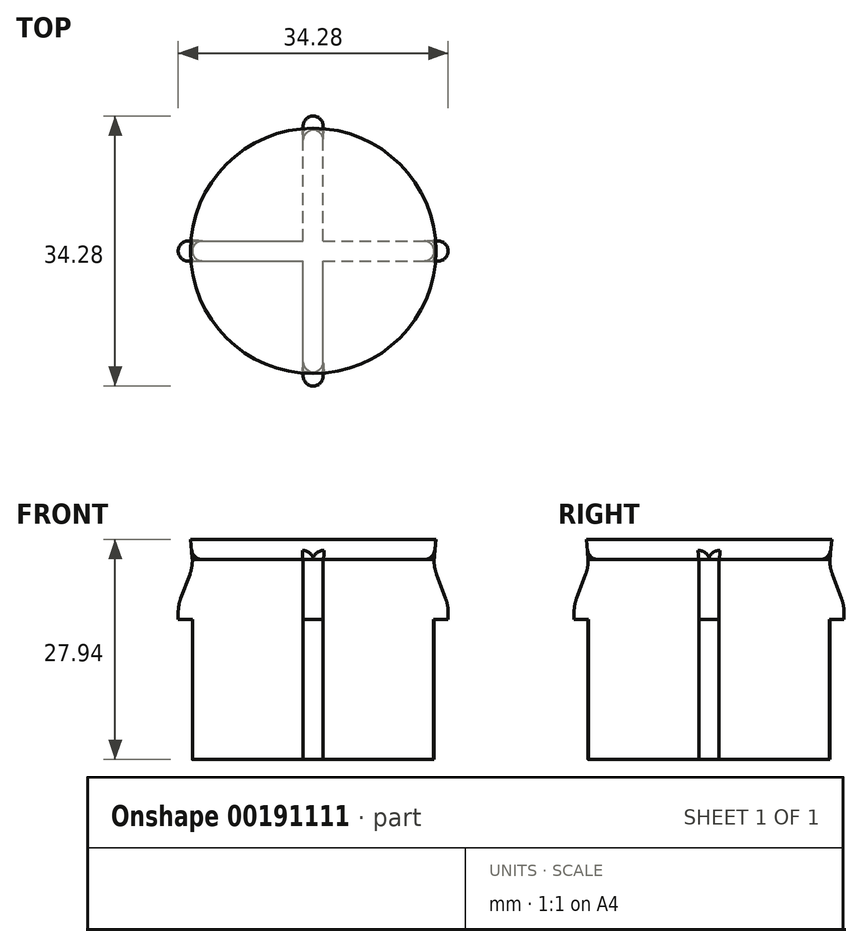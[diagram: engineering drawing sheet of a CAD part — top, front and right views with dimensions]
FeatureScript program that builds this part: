
annotation { "Feature Type Name" : "Feature", "Feature Type Description" : "" }
export const myFeature = defineFeature(function(context is Context, id is Id, definition is map)
    precondition{}
    {
        {
            var Q0;
            Q0=qCreatedBy(makeId("Top.planeOp"),FACE);
            var sketch = newSketch(context, id + "F0", { "sketchPlane" : qUnion([Q0])});
            skCircle(sketch, "E0", {"center": v(0, 0) * mm, "radius": 15.37 * mm});
            skSolve(sketch);
        }
        {
            var Q0;
            Q0 = qSketchRegion(id + "F0", true);
            extrude(context, id + "F1", {"entities" : qUnion([Q0]), "depth" : 2.54 * mm, "hasDraft" : true, "draftAngle" : 5 * degree});
        }
        {
            var Q0;
            Q0=makeQuery(id+"F1.opExtrude","CAP_FACE",FACE,{"disambiguationData":[OSD([sQuery(id+"F0.wireOp",EDGE,"E0")])],"isStart":true});
            var sketch = newSketch(context, id + "F2", { "sketchPlane" : qUnion([Q0])});
            skLineSegment(sketch, "E1.left", {"start": v(-1.27, 15.3) * mm, "end": v(-1.27, 1.27) * mm});
            skLineSegment(sketch, "E1.right", {"start": v(1.27, 15.3) * mm, "end": v(1.27, 1.27) * mm});
            skLineSegment(sketch, "E2.bottom", {"start": v(-15.3, 1.27) * mm, "end": v(-1.27, 1.27) * mm});
            skLineSegment(sketch, "E2.top", {"start": v(-15.3, -1.27) * mm, "end": v(-1.27, -1.27) * mm});
            skLineSegment(sketch, "E3.trimOffspring", {"start": v(1.27, 1.27) * mm, "end": v(15.3, 1.27) * mm});
            skLineSegment(sketch, "E4.trimOffspring", {"start": v(1.27, -1.27) * mm, "end": v(1.27, -15.3) * mm});
            skLineSegment(sketch, "E5.trimOffspring", {"start": v(1.27, -1.27) * mm, "end": v(15.3, -1.27) * mm});
            skLineSegment(sketch, "E6.trimOffspring", {"start": v(-1.27, -1.27) * mm, "end": v(-1.27, -15.3) * mm});
            skArc(sketch, "E7", {"start": v(1.27, 15.3) * mm, "mid": v(0, 15.35) * mm, "end": v(-1.27, 15.3) * mm});
            skArc(sketch, "E8.trimOffspring", {"start": v(15.3, -1.27) * mm, "mid": v(15.35, 0) * mm, "end": v(15.3, 1.27) * mm});
            skArc(sketch, "E9.trimOffspring", {"start": v(-1.27, -15.3) * mm, "mid": v(0, -15.35) * mm, "end": v(1.27, -15.3) * mm});
            skArc(sketch, "E10.trimOffspring", {"start": v(-15.3, 1.27) * mm, "mid": v(-15.35, 0) * mm, "end": v(-15.3, -1.27) * mm});
            skSolve(sketch);
        }
        {
            var Q0;
            Q0 = qSketchRegion(id + "F2", true);
            extrude(context, id + "F3", {"entities" : qUnion([Q0]), "operationType" : NewBodyOperationType.ADD, "depth" : 25.4 * mm});
        }
        {
            var Q0;
            Q0 = qSketchRegion(id + "F2", true);
            extrude(context, id + "F4", {"entities" : qUnion([Q0]), "operationType" : NewBodyOperationType.ADD, "depth" : 25.4 * mm});
        }
        {
            var Q0;
            Q0=qCreatedBy(makeId("Top.planeOp"),FACE);
            cPlane(context, id + "F5", {"entities" : qUnion([Q0]), "cplaneType" : CPlaneType.OFFSET, "offset" : 7.62 * mm, "oppositeDirection" : true, "width" : 152.4 * mm, "height" : 152.4 * mm});
        }
        {
            var Q0;
            Q0=qCreatedBy(id+"F5.planeOp",FACE);
            var sketch = newSketch(context, id + "F6", { "sketchPlane" : qUnion([Q0])});
            skArc(sketch, "E11", {"start": v(-1.27, -17.1) * mm, "mid": v(0, -17.15) * mm, "end": v(1.27, -17.1) * mm});
            skLineSegment(sketch, "E12.left", {"start": v(-1.27, -17.1) * mm, "end": v(-1.27, 17.1) * mm});
            skLineSegment(sketch, "E12.right", {"start": v(1.27, -17.1) * mm, "end": v(1.27, 17.1) * mm});
            skLineSegment(sketch, "E13.bottom", {"start": v(-17.1, -1.27) * mm, "end": v(17.1, -1.27) * mm});
            skLineSegment(sketch, "E13.top", {"start": v(-17.1, 1.27) * mm, "end": v(17.1, 1.27) * mm});
            skArc(sketch, "E14.trimOffspring", {"start": v(17.1, -1.27) * mm, "mid": v(17.15, 0) * mm, "end": v(17.1, 1.27) * mm});
            skArc(sketch, "E15.trimOffspring", {"start": v(1.27, 17.1) * mm, "mid": v(0, 17.15) * mm, "end": v(-1.27, 17.1) * mm});
            skArc(sketch, "E16.trimOffspring", {"start": v(-17.1, 1.27) * mm, "mid": v(-17.15, 0) * mm, "end": v(-17.1, -1.27) * mm});
            skSolve(sketch);
        }
        {
            var Q0;
            Q0 = qSketchRegion(id + "F6", true);
            extrude(context, id + "F7", {"entities" : qUnion([Q0]), "operationType" : NewBodyOperationType.ADD, "depth" : 1.52 * mm});
        }
        {
            var Q0;
            Q0=makeQuery(id+"F7.boolean.opBoolean","INTERSECT",EDGE,{"derivedFrom":[makeQuery(id+"F3.opExtrude","SWEPT_FACE",FACE,{"disambiguationData":[OSD([sQuery(id+"F2.wireOp",EDGE,"E7")])]}),makeQuery(id+"F7.opExtrude","CAP_FACE",FACE,{"disambiguationData":[OSD([sQuery(id+"F6.wireOp",EDGE,"E11"),sQuery(id+"F6.wireOp",EDGE,"E12.left"),sQuery(id+"F6.wireOp",EDGE,"E12.right"),sQuery(id+"F6.wireOp",EDGE,"E13.bottom"),sQuery(id+"F6.wireOp",EDGE,"E13.top"),sQuery(id+"F6.wireOp",EDGE,"E14.trimOffspring"),sQuery(id+"F6.wireOp",EDGE,"E15.trimOffspring"),sQuery(id+"F6.wireOp",EDGE,"E16.trimOffspring")])],"isStart":false})]});
            chamfer(context, id + "F8", {"entities" : qUnion([Q0]), "chamferType" : ChamferType.TWO_OFFSETS, "width1" : 5.08 * mm, "oppositeDirection" : false, "width2" : 1.9 * mm, "tangentPropagation" : true});
        }
        {
            var Q0;
            Q0=makeQuery(id+"F7.boolean.opBoolean","INTERSECT",EDGE,{"derivedFrom":[makeQuery(id+"F3.opExtrude","SWEPT_FACE",FACE,{"disambiguationData":[OSD([sQuery(id+"F2.wireOp",EDGE,"E8.trimOffspring")])]}),makeQuery(id+"F7.opExtrude","CAP_FACE",FACE,{"disambiguationData":[OSD([sQuery(id+"F6.wireOp",EDGE,"E11"),sQuery(id+"F6.wireOp",EDGE,"E12.left"),sQuery(id+"F6.wireOp",EDGE,"E12.right"),sQuery(id+"F6.wireOp",EDGE,"E13.bottom"),sQuery(id+"F6.wireOp",EDGE,"E13.top"),sQuery(id+"F6.wireOp",EDGE,"E14.trimOffspring"),sQuery(id+"F6.wireOp",EDGE,"E15.trimOffspring"),sQuery(id+"F6.wireOp",EDGE,"E16.trimOffspring")])],"isStart":false})]});
            chamfer(context, id + "F9", {"entities" : qUnion([Q0]), "chamferType" : ChamferType.TWO_OFFSETS, "width1" : 5.08 * mm, "oppositeDirection" : false, "width2" : 1.9 * mm, "tangentPropagation" : true});
        }
        {
            var Q0;
            Q0=makeQuery(id+"F7.boolean.opBoolean","INTERSECT",EDGE,{"derivedFrom":[makeQuery(id+"F3.opExtrude","SWEPT_FACE",FACE,{"disambiguationData":[OSD([sQuery(id+"F2.wireOp",EDGE,"E9.trimOffspring")])]}),makeQuery(id+"F7.opExtrude","CAP_FACE",FACE,{"disambiguationData":[OSD([sQuery(id+"F6.wireOp",EDGE,"E11"),sQuery(id+"F6.wireOp",EDGE,"E12.left"),sQuery(id+"F6.wireOp",EDGE,"E12.right"),sQuery(id+"F6.wireOp",EDGE,"E13.bottom"),sQuery(id+"F6.wireOp",EDGE,"E13.top"),sQuery(id+"F6.wireOp",EDGE,"E14.trimOffspring"),sQuery(id+"F6.wireOp",EDGE,"E15.trimOffspring"),sQuery(id+"F6.wireOp",EDGE,"E16.trimOffspring")])],"isStart":false})]});
            chamfer(context, id + "F10", {"entities" : qUnion([Q0]), "chamferType" : ChamferType.TWO_OFFSETS, "width1" : 5.08 * mm, "oppositeDirection" : false, "width2" : 1.9 * mm, "tangentPropagation" : true});
        }
        {
            var Q0;
            Q0=makeQuery(id+"F7.boolean.opBoolean","INTERSECT",EDGE,{"derivedFrom":[makeQuery(id+"F3.opExtrude","SWEPT_FACE",FACE,{"disambiguationData":[OSD([sQuery(id+"F2.wireOp",EDGE,"E10.trimOffspring")])]}),makeQuery(id+"F7.opExtrude","CAP_FACE",FACE,{"disambiguationData":[OSD([sQuery(id+"F6.wireOp",EDGE,"E11"),sQuery(id+"F6.wireOp",EDGE,"E12.left"),sQuery(id+"F6.wireOp",EDGE,"E12.right"),sQuery(id+"F6.wireOp",EDGE,"E13.bottom"),sQuery(id+"F6.wireOp",EDGE,"E13.top"),sQuery(id+"F6.wireOp",EDGE,"E14.trimOffspring"),sQuery(id+"F6.wireOp",EDGE,"E15.trimOffspring"),sQuery(id+"F6.wireOp",EDGE,"E16.trimOffspring")])],"isStart":false})]});
            chamfer(context, id + "F11", {"entities" : qUnion([Q0]), "chamferType" : ChamferType.TWO_OFFSETS, "width1" : 5.08 * mm, "oppositeDirection" : false, "width2" : 1.9 * mm, "tangentPropagation" : true});
        }
        {
            var Q0;
            {var subQ0=sQuery(id+"F6.wireOp",EDGE,"E13.bottom");var subQ1=sQuery(id+"F6.wireOp",EDGE,"E12.right");var subQ2=sQuery(id+"F6.wireOp",EDGE,"E12.left");var subQ3=sQuery(id+"F6.wireOp",EDGE,"E11");var subQ4=makeQuery(id+"F7.opExtrude","CAP_FACE",FACE,{"disambiguationData":[OSD([subQ3,subQ2,subQ1,subQ0,sQuery(id+"F6.wireOp",EDGE,"E13.top"),sQuery(id+"F6.wireOp",EDGE,"E14.trimOffspring"),sQuery(id+"F6.wireOp",EDGE,"E15.trimOffspring"),sQuery(id+"F6.wireOp",EDGE,"E16.trimOffspring")])],"isStart":false});var subQ5=makeQuery(id+"F3.opExtrude","SWEPT_FACE",FACE,{"disambiguationData":[OSD([sQuery(id+"F2.wireOp",EDGE,"E7")])]});Q0=makeQuery(id+"F8.opChamfer","BLEND_EDGE",EDGE,{"blendedFrom":[makeQuery(id+"F7.boolean.opBoolean","INTERSECT",EDGE,{"derivedFrom":[subQ5,subQ4]}),makeQuery(id+"F7.boolean.opBoolean","SPLIT",FACE,{"disambiguationData":[TD([makeQuery(id+"F1.opExtrude","CAP_FACE",FACE,{"disambiguationData":[OSD([sQuery(id+"F0.wireOp",EDGE,"E0")])],"isStart":true})])],"derivedFrom":subQ5})],"blendedInto":[makeQuery(id+"F7.boolean.opBoolean","SPLIT",FACE,{"disambiguationData":[TD([makeQuery(id+"F1.opExtrude","CAP_FACE",FACE,{"disambiguationData":[OSD([sQuery(id+"F0.wireOp",EDGE,"E0")])],"isStart":true})])],"derivedFrom":subQ5})]});}
            var Q1;
            {var subQ0=sQuery(id+"F6.wireOp",EDGE,"E14.trimOffspring");var subQ1=sQuery(id+"F6.wireOp",EDGE,"E13.top");var subQ2=sQuery(id+"F6.wireOp",EDGE,"E13.bottom");var subQ3=sQuery(id+"F6.wireOp",EDGE,"E12.right");var subQ4=makeQuery(id+"F7.opExtrude","CAP_FACE",FACE,{"disambiguationData":[OSD([sQuery(id+"F6.wireOp",EDGE,"E11"),sQuery(id+"F6.wireOp",EDGE,"E12.left"),subQ3,subQ2,subQ1,subQ0,sQuery(id+"F6.wireOp",EDGE,"E15.trimOffspring"),sQuery(id+"F6.wireOp",EDGE,"E16.trimOffspring")])],"isStart":false});var subQ5=makeQuery(id+"F3.opExtrude","SWEPT_FACE",FACE,{"disambiguationData":[OSD([sQuery(id+"F2.wireOp",EDGE,"E8.trimOffspring")])]});Q1=makeQuery(id+"F9.opChamfer","BLEND_EDGE",EDGE,{"blendedFrom":[makeQuery(id+"F7.boolean.opBoolean","INTERSECT",EDGE,{"derivedFrom":[subQ5,subQ4]}),makeQuery(id+"F7.boolean.opBoolean","SPLIT",FACE,{"disambiguationData":[TD([makeQuery(id+"F1.opExtrude","CAP_FACE",FACE,{"disambiguationData":[OSD([sQuery(id+"F0.wireOp",EDGE,"E0")])],"isStart":true})])],"derivedFrom":subQ5})],"blendedInto":[makeQuery(id+"F7.boolean.opBoolean","SPLIT",FACE,{"disambiguationData":[TD([makeQuery(id+"F1.opExtrude","CAP_FACE",FACE,{"disambiguationData":[OSD([sQuery(id+"F0.wireOp",EDGE,"E0")])],"isStart":true})])],"derivedFrom":subQ5})]});}
            var Q2;
            {var subQ0=sQuery(id+"F6.wireOp",EDGE,"E15.trimOffspring");var subQ1=sQuery(id+"F6.wireOp",EDGE,"E13.top");var subQ2=sQuery(id+"F6.wireOp",EDGE,"E12.right");var subQ3=sQuery(id+"F6.wireOp",EDGE,"E12.left");var subQ4=makeQuery(id+"F7.opExtrude","CAP_FACE",FACE,{"disambiguationData":[OSD([sQuery(id+"F6.wireOp",EDGE,"E11"),subQ3,subQ2,sQuery(id+"F6.wireOp",EDGE,"E13.bottom"),subQ1,sQuery(id+"F6.wireOp",EDGE,"E14.trimOffspring"),subQ0,sQuery(id+"F6.wireOp",EDGE,"E16.trimOffspring")])],"isStart":false});var subQ5=makeQuery(id+"F3.opExtrude","SWEPT_FACE",FACE,{"disambiguationData":[OSD([sQuery(id+"F2.wireOp",EDGE,"E9.trimOffspring")])]});Q2=makeQuery(id+"F10.opChamfer","BLEND_EDGE",EDGE,{"blendedFrom":[makeQuery(id+"F7.boolean.opBoolean","INTERSECT",EDGE,{"derivedFrom":[subQ5,subQ4]}),makeQuery(id+"F7.boolean.opBoolean","SPLIT",FACE,{"disambiguationData":[TD([makeQuery(id+"F1.opExtrude","CAP_FACE",FACE,{"disambiguationData":[OSD([sQuery(id+"F0.wireOp",EDGE,"E0")])],"isStart":true})])],"derivedFrom":subQ5})],"blendedInto":[makeQuery(id+"F7.boolean.opBoolean","SPLIT",FACE,{"disambiguationData":[TD([makeQuery(id+"F1.opExtrude","CAP_FACE",FACE,{"disambiguationData":[OSD([sQuery(id+"F0.wireOp",EDGE,"E0")])],"isStart":true})])],"derivedFrom":subQ5})]});}
            var Q3;
            {var subQ0=sQuery(id+"F6.wireOp",EDGE,"E16.trimOffspring");var subQ1=sQuery(id+"F6.wireOp",EDGE,"E13.top");var subQ2=sQuery(id+"F6.wireOp",EDGE,"E13.bottom");var subQ3=sQuery(id+"F6.wireOp",EDGE,"E12.left");var subQ4=makeQuery(id+"F7.opExtrude","CAP_FACE",FACE,{"disambiguationData":[OSD([sQuery(id+"F6.wireOp",EDGE,"E11"),subQ3,sQuery(id+"F6.wireOp",EDGE,"E12.right"),subQ2,subQ1,sQuery(id+"F6.wireOp",EDGE,"E14.trimOffspring"),sQuery(id+"F6.wireOp",EDGE,"E15.trimOffspring"),subQ0])],"isStart":false});var subQ5=makeQuery(id+"F3.opExtrude","SWEPT_FACE",FACE,{"disambiguationData":[OSD([sQuery(id+"F2.wireOp",EDGE,"E10.trimOffspring")])]});Q3=makeQuery(id+"F11.opChamfer","BLEND_EDGE",EDGE,{"blendedFrom":[makeQuery(id+"F7.boolean.opBoolean","INTERSECT",EDGE,{"derivedFrom":[subQ5,subQ4]}),makeQuery(id+"F7.boolean.opBoolean","SPLIT",FACE,{"disambiguationData":[TD([makeQuery(id+"F1.opExtrude","CAP_FACE",FACE,{"disambiguationData":[OSD([sQuery(id+"F0.wireOp",EDGE,"E0")])],"isStart":true})])],"derivedFrom":subQ5})],"blendedInto":[makeQuery(id+"F7.boolean.opBoolean","SPLIT",FACE,{"disambiguationData":[TD([makeQuery(id+"F1.opExtrude","CAP_FACE",FACE,{"disambiguationData":[OSD([sQuery(id+"F0.wireOp",EDGE,"E0")])],"isStart":true})])],"derivedFrom":subQ5})]});}
            fillet(context, id + "F12", {"entities" : qUnion([Q0, Q1, Q2, Q3]), "radius" : 5.08 * mm, "tangentPropagation" : true, "allowEdgeOverflow" : false});
        }
        {
            var Q0;
            {var subQ0=sQuery(id+"F6.wireOp",EDGE,"E11");Q0=makeQuery(id+"F8.opChamfer","BLEND_EDGE",EDGE,{"blendedFrom":[makeQuery(id+"F7.boolean.opBoolean","INTERSECT",EDGE,{"derivedFrom":[makeQuery(id+"F3.opExtrude","SWEPT_FACE",FACE,{"disambiguationData":[OSD([sQuery(id+"F2.wireOp",EDGE,"E7")])]}),makeQuery(id+"F7.opExtrude","CAP_FACE",FACE,{"disambiguationData":[OSD([subQ0,sQuery(id+"F6.wireOp",EDGE,"E12.left"),sQuery(id+"F6.wireOp",EDGE,"E12.right"),sQuery(id+"F6.wireOp",EDGE,"E13.bottom"),sQuery(id+"F6.wireOp",EDGE,"E13.top"),sQuery(id+"F6.wireOp",EDGE,"E14.trimOffspring"),sQuery(id+"F6.wireOp",EDGE,"E15.trimOffspring"),sQuery(id+"F6.wireOp",EDGE,"E16.trimOffspring")])],"isStart":false})]}),makeQuery(id+"F7.opExtrude","SWEPT_FACE",FACE,{"disambiguationData":[OSD([subQ0])]})],"blendedInto":[makeQuery(id+"F7.opExtrude","SWEPT_FACE",FACE,{"disambiguationData":[OSD([subQ0])]})]});}
            var Q1;
            {var subQ0=sQuery(id+"F6.wireOp",EDGE,"E16.trimOffspring");Q1=makeQuery(id+"F11.opChamfer","BLEND_EDGE",EDGE,{"blendedFrom":[makeQuery(id+"F7.boolean.opBoolean","INTERSECT",EDGE,{"derivedFrom":[makeQuery(id+"F3.opExtrude","SWEPT_FACE",FACE,{"disambiguationData":[OSD([sQuery(id+"F2.wireOp",EDGE,"E10.trimOffspring")])]}),makeQuery(id+"F7.opExtrude","CAP_FACE",FACE,{"disambiguationData":[OSD([sQuery(id+"F6.wireOp",EDGE,"E11"),sQuery(id+"F6.wireOp",EDGE,"E12.left"),sQuery(id+"F6.wireOp",EDGE,"E12.right"),sQuery(id+"F6.wireOp",EDGE,"E13.bottom"),sQuery(id+"F6.wireOp",EDGE,"E13.top"),sQuery(id+"F6.wireOp",EDGE,"E14.trimOffspring"),sQuery(id+"F6.wireOp",EDGE,"E15.trimOffspring"),subQ0])],"isStart":false})]}),makeQuery(id+"F7.opExtrude","SWEPT_FACE",FACE,{"disambiguationData":[OSD([subQ0])]})],"blendedInto":[makeQuery(id+"F7.opExtrude","SWEPT_FACE",FACE,{"disambiguationData":[OSD([subQ0])]})]});}
            var Q2;
            {var subQ0=sQuery(id+"F6.wireOp",EDGE,"E15.trimOffspring");Q2=makeQuery(id+"F10.opChamfer","BLEND_EDGE",EDGE,{"blendedFrom":[makeQuery(id+"F7.boolean.opBoolean","INTERSECT",EDGE,{"derivedFrom":[makeQuery(id+"F3.opExtrude","SWEPT_FACE",FACE,{"disambiguationData":[OSD([sQuery(id+"F2.wireOp",EDGE,"E9.trimOffspring")])]}),makeQuery(id+"F7.opExtrude","CAP_FACE",FACE,{"disambiguationData":[OSD([sQuery(id+"F6.wireOp",EDGE,"E11"),sQuery(id+"F6.wireOp",EDGE,"E12.left"),sQuery(id+"F6.wireOp",EDGE,"E12.right"),sQuery(id+"F6.wireOp",EDGE,"E13.bottom"),sQuery(id+"F6.wireOp",EDGE,"E13.top"),sQuery(id+"F6.wireOp",EDGE,"E14.trimOffspring"),subQ0,sQuery(id+"F6.wireOp",EDGE,"E16.trimOffspring")])],"isStart":false})]}),makeQuery(id+"F7.opExtrude","SWEPT_FACE",FACE,{"disambiguationData":[OSD([subQ0])]})],"blendedInto":[makeQuery(id+"F7.opExtrude","SWEPT_FACE",FACE,{"disambiguationData":[OSD([subQ0])]})]});}
            var Q3;
            {var subQ0=sQuery(id+"F6.wireOp",EDGE,"E14.trimOffspring");Q3=makeQuery(id+"F9.opChamfer","BLEND_EDGE",EDGE,{"blendedFrom":[makeQuery(id+"F7.boolean.opBoolean","INTERSECT",EDGE,{"derivedFrom":[makeQuery(id+"F3.opExtrude","SWEPT_FACE",FACE,{"disambiguationData":[OSD([sQuery(id+"F2.wireOp",EDGE,"E8.trimOffspring")])]}),makeQuery(id+"F7.opExtrude","CAP_FACE",FACE,{"disambiguationData":[OSD([sQuery(id+"F6.wireOp",EDGE,"E11"),sQuery(id+"F6.wireOp",EDGE,"E12.left"),sQuery(id+"F6.wireOp",EDGE,"E12.right"),sQuery(id+"F6.wireOp",EDGE,"E13.bottom"),sQuery(id+"F6.wireOp",EDGE,"E13.top"),subQ0,sQuery(id+"F6.wireOp",EDGE,"E15.trimOffspring"),sQuery(id+"F6.wireOp",EDGE,"E16.trimOffspring")])],"isStart":false})]}),makeQuery(id+"F7.opExtrude","SWEPT_FACE",FACE,{"disambiguationData":[OSD([subQ0])]})],"blendedInto":[makeQuery(id+"F7.opExtrude","SWEPT_FACE",FACE,{"disambiguationData":[OSD([subQ0])]})]});}
            fillet(context, id + "F13", {"entities" : qUnion([Q0, Q1, Q2, Q3]), "radius" : 5.08 * mm, "tangentPropagation" : true, "allowEdgeOverflow" : false});
        }
        {
            var Q0;
            {var subQ0=sQuery(id+"F6.wireOp",EDGE,"E14.trimOffspring");var subQ1=sQuery(id+"F6.wireOp",EDGE,"E13.top");var subQ2=sQuery(id+"F6.wireOp",EDGE,"E12.right");Q0=makeQuery(id+"F13.opFillet","BLEND_EDGE",EDGE,{"blendedFrom":[makeQuery(id+"F9.opChamfer","BLEND_EDGE",EDGE,{"blendedFrom":[makeQuery(id+"F7.boolean.opBoolean","INTERSECT",EDGE,{"derivedFrom":[makeQuery(id+"F3.opExtrude","SWEPT_FACE",FACE,{"disambiguationData":[OSD([sQuery(id+"F2.wireOp",EDGE,"E8.trimOffspring")])]}),makeQuery(id+"F7.opExtrude","CAP_FACE",FACE,{"disambiguationData":[OSD([sQuery(id+"F6.wireOp",EDGE,"E11"),sQuery(id+"F6.wireOp",EDGE,"E12.left"),subQ2,sQuery(id+"F6.wireOp",EDGE,"E13.bottom"),subQ1,subQ0,sQuery(id+"F6.wireOp",EDGE,"E15.trimOffspring"),sQuery(id+"F6.wireOp",EDGE,"E16.trimOffspring")])],"isStart":false})]}),makeQuery(id+"F7.opExtrude","SWEPT_FACE",FACE,{"disambiguationData":[OSD([subQ0])]})],"blendedInto":[makeQuery(id+"F7.opExtrude","SWEPT_FACE",FACE,{"disambiguationData":[OSD([subQ0])]})]}),makeQuery(id+"F7.boolean.opBoolean","MERGE",FACE,{"derivedFrom":[makeQuery(id+"F3.opExtrude","SWEPT_FACE",FACE,{"disambiguationData":[OSD([sQuery(id+"F2.wireOp",EDGE,"E5.trimOffspring")])]}),makeQuery(id+"F7.opExtrude","SWEPT_FACE",FACE,{"disambiguationData":[OSD([subQ1]),TDD([makeQuery(id+"F6.imprint","IMPRINT",EDGE,{"disambiguationData":[TD([[makeQuery(id+"F6.imprint","INTERSECT",VERTEX,{"derivedFrom":[subQ1,subQ0]}),1.0]])],"derivedFrom":subQ1})])]})]})],"blendedInto":[makeQuery(id+"F7.boolean.opBoolean","MERGE",FACE,{"derivedFrom":[makeQuery(id+"F3.opExtrude","SWEPT_FACE",FACE,{"disambiguationData":[OSD([sQuery(id+"F2.wireOp",EDGE,"E5.trimOffspring")])]}),makeQuery(id+"F7.opExtrude","SWEPT_FACE",FACE,{"disambiguationData":[OSD([subQ1]),TDD([makeQuery(id+"F6.imprint","IMPRINT",EDGE,{"disambiguationData":[TD([[makeQuery(id+"F6.imprint","INTERSECT",VERTEX,{"derivedFrom":[subQ1,subQ0]}),1.0]])],"derivedFrom":subQ1})])]})]})]});}
            var Q1;
            {var subQ0=sQuery(id+"F6.wireOp",EDGE,"E14.trimOffspring");var subQ1=sQuery(id+"F6.wireOp",EDGE,"E13.bottom");var subQ2=sQuery(id+"F6.wireOp",EDGE,"E12.right");Q1=makeQuery(id+"F13.opFillet","BLEND_EDGE",EDGE,{"blendedFrom":[makeQuery(id+"F9.opChamfer","BLEND_EDGE",EDGE,{"blendedFrom":[makeQuery(id+"F7.boolean.opBoolean","INTERSECT",EDGE,{"derivedFrom":[makeQuery(id+"F3.opExtrude","SWEPT_FACE",FACE,{"disambiguationData":[OSD([sQuery(id+"F2.wireOp",EDGE,"E8.trimOffspring")])]}),makeQuery(id+"F7.opExtrude","CAP_FACE",FACE,{"disambiguationData":[OSD([sQuery(id+"F6.wireOp",EDGE,"E11"),sQuery(id+"F6.wireOp",EDGE,"E12.left"),subQ2,subQ1,sQuery(id+"F6.wireOp",EDGE,"E13.top"),subQ0,sQuery(id+"F6.wireOp",EDGE,"E15.trimOffspring"),sQuery(id+"F6.wireOp",EDGE,"E16.trimOffspring")])],"isStart":false})]}),makeQuery(id+"F7.opExtrude","SWEPT_FACE",FACE,{"disambiguationData":[OSD([subQ0])]})],"blendedInto":[makeQuery(id+"F7.opExtrude","SWEPT_FACE",FACE,{"disambiguationData":[OSD([subQ0])]})]}),makeQuery(id+"F7.boolean.opBoolean","MERGE",FACE,{"derivedFrom":[makeQuery(id+"F3.opExtrude","SWEPT_FACE",FACE,{"disambiguationData":[OSD([sQuery(id+"F2.wireOp",EDGE,"E3.trimOffspring")])]}),makeQuery(id+"F7.opExtrude","SWEPT_FACE",FACE,{"disambiguationData":[OSD([subQ1]),TDD([makeQuery(id+"F6.imprint","IMPRINT",EDGE,{"disambiguationData":[TD([[makeQuery(id+"F6.imprint","INTERSECT",VERTEX,{"derivedFrom":[subQ1,subQ0]}),1.0]])],"derivedFrom":subQ1})])]})]})],"blendedInto":[makeQuery(id+"F7.boolean.opBoolean","MERGE",FACE,{"derivedFrom":[makeQuery(id+"F3.opExtrude","SWEPT_FACE",FACE,{"disambiguationData":[OSD([sQuery(id+"F2.wireOp",EDGE,"E3.trimOffspring")])]}),makeQuery(id+"F7.opExtrude","SWEPT_FACE",FACE,{"disambiguationData":[OSD([subQ1]),TDD([makeQuery(id+"F6.imprint","IMPRINT",EDGE,{"disambiguationData":[TD([[makeQuery(id+"F6.imprint","INTERSECT",VERTEX,{"derivedFrom":[subQ1,subQ0]}),1.0]])],"derivedFrom":subQ1})])]})]})]});}
            var Q2;
            {var subQ0=sQuery(id+"F6.wireOp",EDGE,"E15.trimOffspring");var subQ1=sQuery(id+"F6.wireOp",EDGE,"E12.right");var subQ2=sQuery(id+"F6.wireOp",EDGE,"E13.top");Q2=makeQuery(id+"F10.opChamfer","BLEND_EDGE",EDGE,{"blendedFrom":[makeQuery(id+"F7.boolean.opBoolean","INTERSECT",EDGE,{"derivedFrom":[makeQuery(id+"F3.opExtrude","SWEPT_FACE",FACE,{"disambiguationData":[OSD([sQuery(id+"F2.wireOp",EDGE,"E9.trimOffspring")])]}),makeQuery(id+"F7.opExtrude","CAP_FACE",FACE,{"disambiguationData":[OSD([sQuery(id+"F6.wireOp",EDGE,"E11"),sQuery(id+"F6.wireOp",EDGE,"E12.left"),subQ1,sQuery(id+"F6.wireOp",EDGE,"E13.bottom"),subQ2,sQuery(id+"F6.wireOp",EDGE,"E14.trimOffspring"),subQ0,sQuery(id+"F6.wireOp",EDGE,"E16.trimOffspring")])],"isStart":false})]}),makeQuery(id+"F7.boolean.opBoolean","MERGE",FACE,{"derivedFrom":[makeQuery(id+"F3.opExtrude","SWEPT_FACE",FACE,{"disambiguationData":[OSD([sQuery(id+"F2.wireOp",EDGE,"E4.trimOffspring")])]}),makeQuery(id+"F7.opExtrude","SWEPT_FACE",FACE,{"disambiguationData":[OSD([subQ1]),TDD([makeQuery(id+"F6.imprint","IMPRINT",EDGE,{"disambiguationData":[TD([[makeQuery(id+"F6.imprint","INTERSECT",VERTEX,{"derivedFrom":[subQ1,subQ0]}),1.0]])],"derivedFrom":subQ1})])]})]})],"blendedInto":[makeQuery(id+"F7.boolean.opBoolean","MERGE",FACE,{"derivedFrom":[makeQuery(id+"F3.opExtrude","SWEPT_FACE",FACE,{"disambiguationData":[OSD([sQuery(id+"F2.wireOp",EDGE,"E4.trimOffspring")])]}),makeQuery(id+"F7.opExtrude","SWEPT_FACE",FACE,{"disambiguationData":[OSD([subQ1]),TDD([makeQuery(id+"F6.imprint","IMPRINT",EDGE,{"disambiguationData":[TD([[makeQuery(id+"F6.imprint","INTERSECT",VERTEX,{"derivedFrom":[subQ1,subQ0]}),1.0]])],"derivedFrom":subQ1})])]})]})]});}
            var Q3;
            {var subQ0=sQuery(id+"F6.wireOp",EDGE,"E15.trimOffspring");var subQ1=sQuery(id+"F6.wireOp",EDGE,"E12.left");var subQ2=sQuery(id+"F6.wireOp",EDGE,"E13.top");Q3=makeQuery(id+"F10.opChamfer","BLEND_EDGE",EDGE,{"blendedFrom":[makeQuery(id+"F7.boolean.opBoolean","INTERSECT",EDGE,{"derivedFrom":[makeQuery(id+"F3.opExtrude","SWEPT_FACE",FACE,{"disambiguationData":[OSD([sQuery(id+"F2.wireOp",EDGE,"E9.trimOffspring")])]}),makeQuery(id+"F7.opExtrude","CAP_FACE",FACE,{"disambiguationData":[OSD([sQuery(id+"F6.wireOp",EDGE,"E11"),subQ1,sQuery(id+"F6.wireOp",EDGE,"E12.right"),sQuery(id+"F6.wireOp",EDGE,"E13.bottom"),subQ2,sQuery(id+"F6.wireOp",EDGE,"E14.trimOffspring"),subQ0,sQuery(id+"F6.wireOp",EDGE,"E16.trimOffspring")])],"isStart":false})]}),makeQuery(id+"F7.boolean.opBoolean","MERGE",FACE,{"derivedFrom":[makeQuery(id+"F3.opExtrude","SWEPT_FACE",FACE,{"disambiguationData":[OSD([sQuery(id+"F2.wireOp",EDGE,"E6.trimOffspring")])]}),makeQuery(id+"F7.opExtrude","SWEPT_FACE",FACE,{"disambiguationData":[OSD([subQ1]),TDD([makeQuery(id+"F6.imprint","IMPRINT",EDGE,{"disambiguationData":[TD([[makeQuery(id+"F6.imprint","INTERSECT",VERTEX,{"derivedFrom":[subQ1,subQ0]}),1.0]])],"derivedFrom":subQ1})])]})]})],"blendedInto":[makeQuery(id+"F7.boolean.opBoolean","MERGE",FACE,{"derivedFrom":[makeQuery(id+"F3.opExtrude","SWEPT_FACE",FACE,{"disambiguationData":[OSD([sQuery(id+"F2.wireOp",EDGE,"E6.trimOffspring")])]}),makeQuery(id+"F7.opExtrude","SWEPT_FACE",FACE,{"disambiguationData":[OSD([subQ1]),TDD([makeQuery(id+"F6.imprint","IMPRINT",EDGE,{"disambiguationData":[TD([[makeQuery(id+"F6.imprint","INTERSECT",VERTEX,{"derivedFrom":[subQ1,subQ0]}),1.0]])],"derivedFrom":subQ1})])]})]})]});}
            var Q4;
            {var subQ0=sQuery(id+"F6.wireOp",EDGE,"E16.trimOffspring");var subQ1=sQuery(id+"F6.wireOp",EDGE,"E13.top");var subQ2=sQuery(id+"F6.wireOp",EDGE,"E12.left");Q4=makeQuery(id+"F13.opFillet","BLEND_EDGE",EDGE,{"blendedFrom":[makeQuery(id+"F11.opChamfer","BLEND_EDGE",EDGE,{"blendedFrom":[makeQuery(id+"F7.boolean.opBoolean","INTERSECT",EDGE,{"derivedFrom":[makeQuery(id+"F3.opExtrude","SWEPT_FACE",FACE,{"disambiguationData":[OSD([sQuery(id+"F2.wireOp",EDGE,"E10.trimOffspring")])]}),makeQuery(id+"F7.opExtrude","CAP_FACE",FACE,{"disambiguationData":[OSD([sQuery(id+"F6.wireOp",EDGE,"E11"),subQ2,sQuery(id+"F6.wireOp",EDGE,"E12.right"),sQuery(id+"F6.wireOp",EDGE,"E13.bottom"),subQ1,sQuery(id+"F6.wireOp",EDGE,"E14.trimOffspring"),sQuery(id+"F6.wireOp",EDGE,"E15.trimOffspring"),subQ0])],"isStart":false})]}),makeQuery(id+"F7.opExtrude","SWEPT_FACE",FACE,{"disambiguationData":[OSD([subQ0])]})],"blendedInto":[makeQuery(id+"F7.opExtrude","SWEPT_FACE",FACE,{"disambiguationData":[OSD([subQ0])]})]}),makeQuery(id+"F7.boolean.opBoolean","MERGE",FACE,{"derivedFrom":[makeQuery(id+"F3.opExtrude","SWEPT_FACE",FACE,{"disambiguationData":[OSD([sQuery(id+"F2.wireOp",EDGE,"E2.top")])]}),makeQuery(id+"F7.opExtrude","SWEPT_FACE",FACE,{"disambiguationData":[OSD([subQ1]),TDD([makeQuery(id+"F6.imprint","IMPRINT",EDGE,{"disambiguationData":[TD([[makeQuery(id+"F6.imprint","INTERSECT",VERTEX,{"derivedFrom":[subQ1,subQ0]}),-1.0]])],"derivedFrom":subQ1})])]})]})],"blendedInto":[makeQuery(id+"F7.boolean.opBoolean","MERGE",FACE,{"derivedFrom":[makeQuery(id+"F3.opExtrude","SWEPT_FACE",FACE,{"disambiguationData":[OSD([sQuery(id+"F2.wireOp",EDGE,"E2.top")])]}),makeQuery(id+"F7.opExtrude","SWEPT_FACE",FACE,{"disambiguationData":[OSD([subQ1]),TDD([makeQuery(id+"F6.imprint","IMPRINT",EDGE,{"disambiguationData":[TD([[makeQuery(id+"F6.imprint","INTERSECT",VERTEX,{"derivedFrom":[subQ1,subQ0]}),-1.0]])],"derivedFrom":subQ1})])]})]})]});}
            var Q5;
            {var subQ0=sQuery(id+"F6.wireOp",EDGE,"E16.trimOffspring");var subQ1=sQuery(id+"F6.wireOp",EDGE,"E13.bottom");var subQ2=sQuery(id+"F6.wireOp",EDGE,"E12.left");Q5=makeQuery(id+"F11.opChamfer","BLEND_EDGE",EDGE,{"blendedFrom":[makeQuery(id+"F7.boolean.opBoolean","INTERSECT",EDGE,{"derivedFrom":[makeQuery(id+"F3.opExtrude","SWEPT_FACE",FACE,{"disambiguationData":[OSD([sQuery(id+"F2.wireOp",EDGE,"E10.trimOffspring")])]}),makeQuery(id+"F7.opExtrude","CAP_FACE",FACE,{"disambiguationData":[OSD([sQuery(id+"F6.wireOp",EDGE,"E11"),subQ2,sQuery(id+"F6.wireOp",EDGE,"E12.right"),subQ1,sQuery(id+"F6.wireOp",EDGE,"E13.top"),sQuery(id+"F6.wireOp",EDGE,"E14.trimOffspring"),sQuery(id+"F6.wireOp",EDGE,"E15.trimOffspring"),subQ0])],"isStart":false})]}),makeQuery(id+"F7.boolean.opBoolean","MERGE",FACE,{"derivedFrom":[makeQuery(id+"F3.opExtrude","SWEPT_FACE",FACE,{"disambiguationData":[OSD([sQuery(id+"F2.wireOp",EDGE,"E2.bottom")])]}),makeQuery(id+"F7.opExtrude","SWEPT_FACE",FACE,{"disambiguationData":[OSD([subQ1]),TDD([makeQuery(id+"F6.imprint","IMPRINT",EDGE,{"disambiguationData":[TD([[makeQuery(id+"F6.imprint","INTERSECT",VERTEX,{"derivedFrom":[subQ1,subQ0]}),-1.0]])],"derivedFrom":subQ1})])]})]})],"blendedInto":[makeQuery(id+"F7.boolean.opBoolean","MERGE",FACE,{"derivedFrom":[makeQuery(id+"F3.opExtrude","SWEPT_FACE",FACE,{"disambiguationData":[OSD([sQuery(id+"F2.wireOp",EDGE,"E2.bottom")])]}),makeQuery(id+"F7.opExtrude","SWEPT_FACE",FACE,{"disambiguationData":[OSD([subQ1]),TDD([makeQuery(id+"F6.imprint","IMPRINT",EDGE,{"disambiguationData":[TD([[makeQuery(id+"F6.imprint","INTERSECT",VERTEX,{"derivedFrom":[subQ1,subQ0]}),-1.0]])],"derivedFrom":subQ1})])]})]})]});}
            var Q6;
            {var subQ0=sQuery(id+"F6.wireOp",EDGE,"E12.left");var subQ1=sQuery(id+"F6.wireOp",EDGE,"E11");var subQ2=sQuery(id+"F6.wireOp",EDGE,"E13.bottom");Q6=makeQuery(id+"F8.opChamfer","BLEND_EDGE",EDGE,{"blendedFrom":[makeQuery(id+"F7.boolean.opBoolean","INTERSECT",EDGE,{"derivedFrom":[makeQuery(id+"F3.opExtrude","SWEPT_FACE",FACE,{"disambiguationData":[OSD([sQuery(id+"F2.wireOp",EDGE,"E7")])]}),makeQuery(id+"F7.opExtrude","CAP_FACE",FACE,{"disambiguationData":[OSD([subQ1,subQ0,sQuery(id+"F6.wireOp",EDGE,"E12.right"),subQ2,sQuery(id+"F6.wireOp",EDGE,"E13.top"),sQuery(id+"F6.wireOp",EDGE,"E14.trimOffspring"),sQuery(id+"F6.wireOp",EDGE,"E15.trimOffspring"),sQuery(id+"F6.wireOp",EDGE,"E16.trimOffspring")])],"isStart":false})]}),makeQuery(id+"F7.boolean.opBoolean","MERGE",FACE,{"derivedFrom":[makeQuery(id+"F3.opExtrude","SWEPT_FACE",FACE,{"disambiguationData":[OSD([sQuery(id+"F2.wireOp",EDGE,"E1.left")])]}),makeQuery(id+"F7.opExtrude","SWEPT_FACE",FACE,{"disambiguationData":[OSD([subQ0]),TDD([makeQuery(id+"F6.imprint","IMPRINT",EDGE,{"disambiguationData":[TD([[makeQuery(id+"F6.imprint","INTERSECT",VERTEX,{"derivedFrom":[subQ1,subQ0]}),-1.0]])],"derivedFrom":subQ0})])]})]})],"blendedInto":[makeQuery(id+"F7.boolean.opBoolean","MERGE",FACE,{"derivedFrom":[makeQuery(id+"F3.opExtrude","SWEPT_FACE",FACE,{"disambiguationData":[OSD([sQuery(id+"F2.wireOp",EDGE,"E1.left")])]}),makeQuery(id+"F7.opExtrude","SWEPT_FACE",FACE,{"disambiguationData":[OSD([subQ0]),TDD([makeQuery(id+"F6.imprint","IMPRINT",EDGE,{"disambiguationData":[TD([[makeQuery(id+"F6.imprint","INTERSECT",VERTEX,{"derivedFrom":[subQ1,subQ0]}),-1.0]])],"derivedFrom":subQ0})])]})]})]});}
            var Q7;
            {var subQ0=sQuery(id+"F6.wireOp",EDGE,"E12.right");var subQ1=sQuery(id+"F6.wireOp",EDGE,"E11");var subQ2=sQuery(id+"F6.wireOp",EDGE,"E13.bottom");Q7=makeQuery(id+"F8.opChamfer","BLEND_EDGE",EDGE,{"blendedFrom":[makeQuery(id+"F7.boolean.opBoolean","INTERSECT",EDGE,{"derivedFrom":[makeQuery(id+"F3.opExtrude","SWEPT_FACE",FACE,{"disambiguationData":[OSD([sQuery(id+"F2.wireOp",EDGE,"E7")])]}),makeQuery(id+"F7.opExtrude","CAP_FACE",FACE,{"disambiguationData":[OSD([subQ1,sQuery(id+"F6.wireOp",EDGE,"E12.left"),subQ0,subQ2,sQuery(id+"F6.wireOp",EDGE,"E13.top"),sQuery(id+"F6.wireOp",EDGE,"E14.trimOffspring"),sQuery(id+"F6.wireOp",EDGE,"E15.trimOffspring"),sQuery(id+"F6.wireOp",EDGE,"E16.trimOffspring")])],"isStart":false})]}),makeQuery(id+"F7.boolean.opBoolean","MERGE",FACE,{"derivedFrom":[makeQuery(id+"F3.opExtrude","SWEPT_FACE",FACE,{"disambiguationData":[OSD([sQuery(id+"F2.wireOp",EDGE,"E1.right")])]}),makeQuery(id+"F7.opExtrude","SWEPT_FACE",FACE,{"disambiguationData":[OSD([subQ0]),TDD([makeQuery(id+"F6.imprint","IMPRINT",EDGE,{"disambiguationData":[TD([[makeQuery(id+"F6.imprint","INTERSECT",VERTEX,{"derivedFrom":[subQ1,subQ0]}),-1.0]])],"derivedFrom":subQ0})])]})]})],"blendedInto":[makeQuery(id+"F7.boolean.opBoolean","MERGE",FACE,{"derivedFrom":[makeQuery(id+"F3.opExtrude","SWEPT_FACE",FACE,{"disambiguationData":[OSD([sQuery(id+"F2.wireOp",EDGE,"E1.right")])]}),makeQuery(id+"F7.opExtrude","SWEPT_FACE",FACE,{"disambiguationData":[OSD([subQ0]),TDD([makeQuery(id+"F6.imprint","IMPRINT",EDGE,{"disambiguationData":[TD([[makeQuery(id+"F6.imprint","INTERSECT",VERTEX,{"derivedFrom":[subQ1,subQ0]}),-1.0]])],"derivedFrom":subQ0})])]})]})]});}
            fillet(context, id + "F14", {"entities" : qUnion([Q0, Q1, Q2, Q3, Q4, Q5, Q6, Q7]), "radius" : 1.27 * mm, "tangentPropagation" : true, "allowEdgeOverflow" : false});
        }
        {
            var Q0;
            Q0=makeQuery(id+"F1.opExtrude","CAP_EDGE",EDGE,{"disambiguationData":[OSD([sQuery(id+"F0.wireOp",EDGE,"E0")])],"isStart":true});
            fillet(context, id + "F15", {"entities" : qUnion([Q0]), "radius" : 1.27 * mm, "tangentPropagation" : true, "allowEdgeOverflow" : false});
        }
    });
